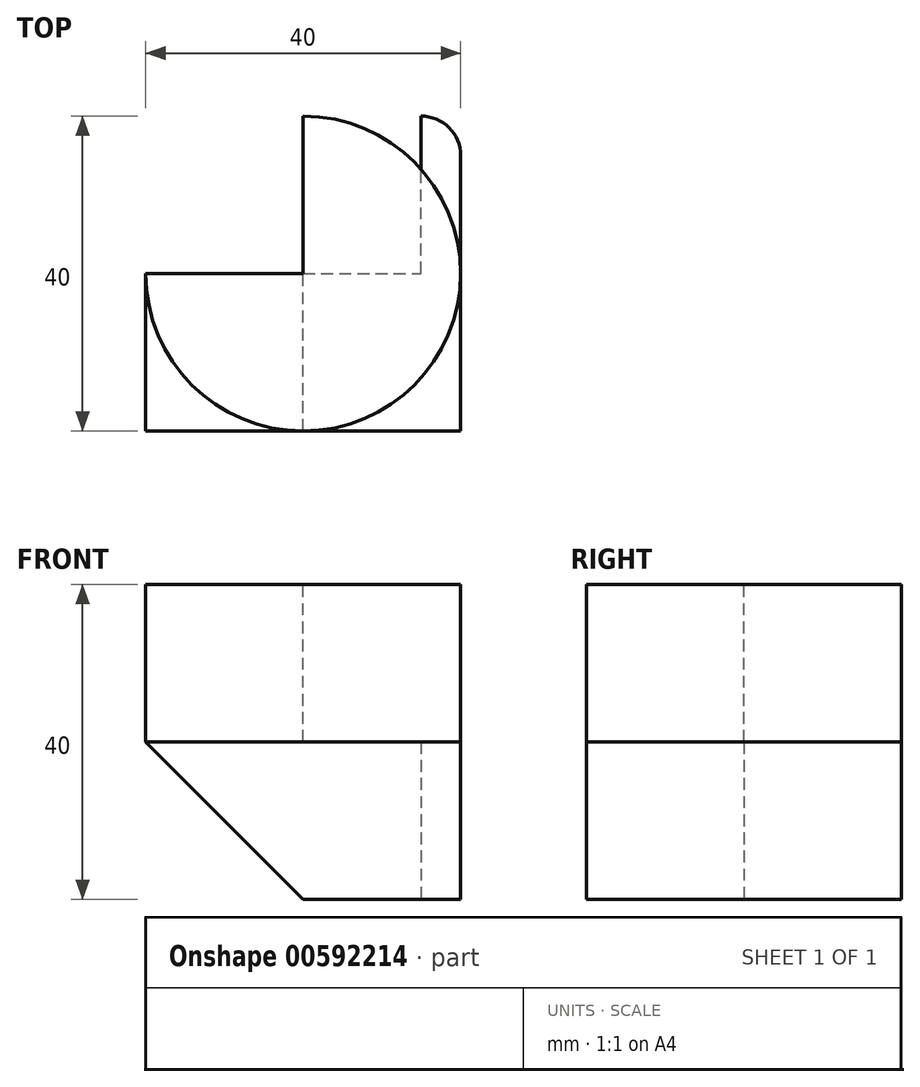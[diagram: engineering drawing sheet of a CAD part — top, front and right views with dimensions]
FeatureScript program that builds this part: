
annotation { "Feature Type Name" : "Feature", "Feature Type Description" : "" }
export const myFeature = defineFeature(function(context is Context, id is Id, definition is map)
    precondition{}
    {
        {
            var Q0;
            Q0=qCreatedBy(makeId("Top.planeOp"),FACE);
            var sketch = newSketch(context, id + "F0", { "sketchPlane" : qUnion([Q0])});
            skCircle(sketch, "E0", {"center": v(0, 0) * mm, "radius": 20 * mm});
            skLineSegment(sketch, "E1", {"start": v(-20, 20) * mm, "end": v(15, 20) * mm});
            skLineSegment(sketch, "E2", {"start": v(20, 15) * mm, "end": v(20, -20) * mm});
            skLineSegment(sketch, "E3", {"start": v(20, -20) * mm, "end": v(-20, -20) * mm});
            skLineSegment(sketch, "E4", {"start": v(-20, 20) * mm, "end": v(-20, -20) * mm});
            skPoint(sketch, "E5.visualSharp", {"position": v(20, 20) * mm});
            skArc(sketch, "E5.filletArc", {"start": v(20, 15) * mm, "mid": v(18.54, 18.54) * mm, "end": v(15, 20) * mm});
            skSolve(sketch);
        }
        {
            var Q0;
            {var subQ0=sQuery(id+"F0.wireOp",EDGE,"E0");var subQ1=makeQuery(id+"F0.imprint","INTERSECT",VERTEX,{"derivedFrom":[subQ0,sQuery(id+"F0.wireOp",EDGE,"E1")]});Q0=makeQuery(id+"F0.imprint","IMPRINT",FACE,{"disambiguationData":[TD([[makeQuery(id+"F0.imprint","IMPRINT",EDGE,{"disambiguationData":[TD([[subQ1,1.0]])],"derivedFrom":subQ0}),1.0]])]});}
            extrude(context, id + "F1", {"entities" : qUnion([Q0]), "depth" : 40 * mm, "offsetDistance" : 25 * mm});
        }
        {
            var Q0;
            {var subQ0=sQuery(id+"F0.wireOp",EDGE,"E1");var subQ1=sQuery(id+"F0.wireOp",EDGE,"E0");var subQ2=makeQuery(id+"F0.imprint","INTERSECT",VERTEX,{"derivedFrom":[subQ1,subQ0]});Q0=makeQuery(id+"F0.imprint","IMPRINT",FACE,{"disambiguationData":[TD([[makeQuery(id+"F0.imprint","IMPRINT",EDGE,{"disambiguationData":[TD([[subQ2,-1.0]])],"derivedFrom":subQ1}),-1.0]])]});}
            var Q1;
            {var subQ5=sQuery(id+"F0.wireOp",EDGE,"E5.filletArc");Q1=makeQuery(id+"F0.imprint","IMPRINT",FACE,{"disambiguationData":[TD([[makeQuery(id+"F0.imprint","IMPRINT",EDGE,{"derivedFrom":subQ5}),1.0]])]});}
            var Q2;
            {var subQ0=sQuery(id+"F0.wireOp",EDGE,"E2");var subQ1=sQuery(id+"F0.wireOp",EDGE,"E0");var subQ2=makeQuery(id+"F0.imprint","INTERSECT",VERTEX,{"derivedFrom":[subQ1,subQ0]});Q2=makeQuery(id+"F0.imprint","IMPRINT",FACE,{"disambiguationData":[TD([[makeQuery(id+"F0.imprint","IMPRINT",EDGE,{"disambiguationData":[TD([[subQ2,1.0]])],"derivedFrom":subQ1}),-1.0]])]});}
            var Q3;
            {var subQ0=sQuery(id+"F0.wireOp",EDGE,"E4");var subQ1=sQuery(id+"F0.wireOp",EDGE,"E0");var subQ2=makeQuery(id+"F0.imprint","INTERSECT",VERTEX,{"derivedFrom":[subQ1,subQ0]});Q3=makeQuery(id+"F0.imprint","IMPRINT",FACE,{"disambiguationData":[TD([[makeQuery(id+"F0.imprint","IMPRINT",EDGE,{"disambiguationData":[TD([[subQ2,-1.0]])],"derivedFrom":subQ1}),-1.0]])]});}
            extrude(context, id + "F2", {"entities" : qUnion([Q0, Q1, Q2, Q3]), "depth" : 20 * mm, "offsetDistance" : 25 * mm});
        }
        {
            var Q0;
            {var subQ0=sQuery(id+"F0.wireOp",EDGE,"E3");Q0=makeQuery(id+"F2.opExtrude","SWEPT_FACE",FACE,{"disambiguationData":[OSD([subQ0]),TDD([makeQuery(id+"F0.imprint","IMPRINT",EDGE,{"disambiguationData":[TD([[makeQuery(id+"F0.imprint","INTERSECT",VERTEX,{"derivedFrom":[subQ0,sQuery(id+"F0.wireOp",EDGE,"E4")]}),1.0]])],"derivedFrom":subQ0})])]});}
            var sketch = newSketch(context, id + "F3", { "sketchPlane" : qUnion([Q0])});
            skLineSegment(sketch, "E6", {"start": v(0, 0) * mm, "end": v(-20, 20) * mm});
            skLineSegment(sketch, "E7", {"start": v(-20, 20) * mm, "end": v(0, 40) * mm});
            skSolve(sketch);
        }
        {
            var Q0;
            Q0=makeQuery(id+"F3.imprint","IMPRINT",FACE,{"disambiguationData":[TD([[makeQuery(id+"F3.imprint","IMPRINT",EDGE,{"derivedFrom":sQuery(id+"F3.wireOp",EDGE,"E6")}),1.0]])]});
            extrude(context, id + "F4", {"entities" : qUnion([Q0]), "operationType" : NewBodyOperationType.ADD, "depth" : 18.7 * mm, "offsetDistance" : 25 * mm});
        }
        {
            var Q0;
            Q0=makeQuery(id+"F4.opExtrude","CAP_FACE",FACE,{"disambiguationData":[OSD([sQuery(id+"F0.wireOp",EDGE,"E3"),sQuery(id+"F0.wireOp",EDGE,"E4"),sQuery(id+"F3.wireOp",EDGE,"E6")])],"isStart":false});
            extrude(context, id + "F5", {"entities" : qUnion([Q0]), "operationType" : NewBodyOperationType.ADD, "oppositeDirection" : true, "depth" : 77.7 * mm, "offsetDistance" : 25 * mm});
        }
        {
            var Q0;
            Q0=makeQuery(id+"F5.opExtrude","CAP_FACE",FACE,{"disambiguationData":[OSD([sQuery(id+"F0.wireOp",EDGE,"E3"),sQuery(id+"F0.wireOp",EDGE,"E4"),sQuery(id+"F3.wireOp",EDGE,"E6")])],"isStart":false});
            extrude(context, id + "F6", {"entities" : qUnion([Q0]), "operationType" : NewBodyOperationType.REMOVE, "oppositeDirection" : true, "depth" : 84.4 * mm, "offsetDistance" : 25 * mm});
        }
        {
            var Q0;
            Q0=makeQuery(id+"F1.opExtrude","CAP_FACE",FACE,{"disambiguationData":[OSD([sQuery(id+"F0.wireOp",EDGE,"E0")])],"isStart":false});
            var sketch = newSketch(context, id + "F7", { "sketchPlane" : qUnion([Q0])});
            skLineSegment(sketch, "E8", {"start": v(0, 0) * mm, "end": v(-20, 0) * mm});
            skLineSegment(sketch, "E9", {"start": v(0, 0) * mm, "end": v(0, 20) * mm});
            skSolve(sketch);
        }
        {
            var Q0;
            {var subQ0=sQuery(id+"F7.wireOp",EDGE,"E8");Q0=makeQuery(id+"F7.imprint","IMPRINT",FACE,{"disambiguationData":[TD([[makeQuery(id+"F7.imprint","IMPRINT",EDGE,{"derivedFrom":subQ0}),-1.0]])]});}
            extrude(context, id + "F8", {"entities" : qUnion([Q0]), "operationType" : NewBodyOperationType.REMOVE, "oppositeDirection" : true, "depth" : 20 * mm, "offsetDistance" : 25 * mm});
        }
        {
            var Q0;
            {var subQ0=sQuery(id+"F0.wireOp",EDGE,"E1");Q0=makeQuery(id+"F2.opExtrude","SWEPT_FACE",FACE,{"disambiguationData":[OSD([subQ0]),TDD([makeQuery(id+"F0.imprint","IMPRINT",EDGE,{"disambiguationData":[TD([[makeQuery(id+"F0.imprint","INTERSECT",VERTEX,{"derivedFrom":[subQ0,sQuery(id+"F0.wireOp",EDGE,"E4")]}),-1.0]])],"derivedFrom":subQ0})])]});}
            var sketch = newSketch(context, id + "F9", { "sketchPlane" : qUnion([Q0])});
            skLineSegment(sketch, "E10", {"start": v(0, 0) * mm, "end": v(20, 20) * mm});
            skSolve(sketch);
        }
        {
            var Q0;
            Q0 = qSketchRegion(id + "F9", true);
            var Q1;
            Q1=makeQuery(id+"F9.imprint","IMPRINT",FACE,{"disambiguationData":[TD([[makeQuery(id+"F9.imprint","IMPRINT",EDGE,{"derivedFrom":sQuery(id+"F9.wireOp",EDGE,"E10")}),-1.0]])]});
            extrude(context, id + "F10", {"entities" : qUnion([Q0, Q1]), "operationType" : NewBodyOperationType.REMOVE, "oppositeDirection" : true, "depth" : 20 * mm, "offsetDistance" : 25 * mm});
        }
    });
